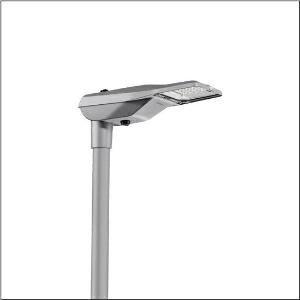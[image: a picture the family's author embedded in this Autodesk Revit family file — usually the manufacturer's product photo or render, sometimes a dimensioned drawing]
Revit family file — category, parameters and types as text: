
# Revit family: streetlight_sl_21_micro___p0_8a_5xe1u33t08db_8449
name_source: partatom
category: Lighting Fixtures
units: mm (PartAtom-declared; Revit-internal decimal feet)

## family parameters
Cut with Voids When Loaded = No
Host = Face
Light Source = No
Part Type = Normal
Room Calculation Point = No
Round Connector Dimension = Use Diameter
Shared = No

## types (1)
- --- (1 x LED, 5040 lm, 39.1 W, 3000K)
    Apparent Load = 39 VA
    CIE Flux Codes = 33 69 96 100 100
    Color Rendering = 70
    Color Temperature = 3000K
    Default Elevation = 1800 mm
    Description = Streetlight SL 21 micro, mast luminaire, primary light control with lens, of PMMA, primary optical cover: cover, of toughened safety glass, transparent, light distribution: P0.8a, light emission: direct distribution, primary light characteristic: asymmetric, installation type: post-top, side-entry, LED, High Power LED, rated luminous flux: 5.040lm, luminous efficacy: 129lm/W, light colour: 730, colour temperature: 3000K, control gear: D4i, control: pre-setting: logarithmic dimming characteristic, flexible luminous flux parameterisation, time-dependent luminous flux control, constant luminous flux control, overheat protection, mains connection: 220..240V, AC, 50/60Hz, start of lifetime: 39W, end of service life: 41W, reduction: 18W, luminaire housing, of diecast aluminium, powder-coated, SITECO metallic grey (DB 702S), corrosivity category C5 high according to DIN EN ISO 12944, multi-level sealing system, sealing non-destructively replaceable, inclination adjustable: 0°, 5°, 10°, 15°, please order mast flange separately, length: 528mm, width: 235mm, height: 110mm, mast flange for spigot size: 42mm (side-entry): 5XC10008XM4, 60/48mm (side-entry/post-top): 5XC10108XM2, 76/60mm (side-entry/post-top): 5XC10108XM1, Smart Interface below and above, protection rating (complete): IP66, insulation class (complete): insulation class II (safety insulation), certification: CE, ENEC, ENEC+, VDE, impact resistance: IK10, permissible operating ambient temperature for outdoor applications: -40..+50°C, standard-compliant lighting for roads and squares, packaging unit: 1 piece

Light Distribution: P0.8a
    Height = 110 mm
    Lamp = 1 x LED
    Lamp Light Flux = 5040 lm
    Lamp Power = 39.1 W
    Lamp count = 1
    Length = 528 mm
    Luminous efficacy = 129 lm/W
    Manufacturer = Siteco
    ModVariant = No
    Model = 5XE1U33T08DB
    Mounting Place = Pole
    Mounting Type = Pole top
    Number of Poles = 1
    OnlyDefault = Yes
    Power Factor = 1
    Product Name = Streetlight SL 21 micro | P0.8a
    Product group = mast luminaire | pylon top
    ProductGroupID = 6100
    Protection Class = Protection class II
    Protection Degree = IP 66
    RLX_Detail_Level = 1
    RLX_Emergency_Light_Flux = 0 lm
    RLX_Emergency_Type = 0
    RLX_Emergency_Type_DB = No
    RlxData = <blob elided: 97577 chars, md5=2cfcc03c>
    Socket = socket
    Standby Power = 0 W
    System Light Flux = 5040 lm
    System Power = 39 W
    Type Comments = factory setting: luminous flux: 100 % | dim-lin: 254 | 765 mA
    Type Image = l_1007239.jpg
    URL = http://relux.com
    VarID = @adj_082079
    Voltage = 0 V
    Weight = 0.00 kg
    Width = 235 mm

## geometry (parser evidence)
native form markers: Blend x4, Sweep x11
no freeform markers — native parametric forms only
